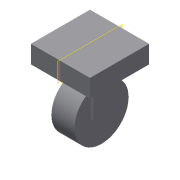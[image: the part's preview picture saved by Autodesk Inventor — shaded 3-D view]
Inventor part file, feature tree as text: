
AUTODESK INVENTOR PART (.ipt)
format: ipt  version: 2019 (Build 230136000, 136)  size: 114,688 bytes
history: native  units: mm
features: extrude x4, sketch x4, other x2, projected_geometry x1
ambient origin geometry x8: Origin, YZ Plane, XZ Plane, XY Plane, X Axis, Y Axis, Z Axis, Center Point
bodies: Body1 (feature_tree), Body2 (feature_tree)
feature tree (11):
  other  "솔리드1"
  extrude  "돌출1"  Depth=24.7mm
  other  "작업 평면1"
  extrude  "돌출2"  Depth=82.0mm
  extrude  "돌출3"  Depth=82.0mm TaperAngle=0.0deg
  extrude  "돌출4"  Depth=50.0mm
  sketch  "스케치1"
  sketch  "스케치2"
  projected_geometry  "투영된 루프1"
  sketch  "스케치3"
  sketch  "스케치4"
